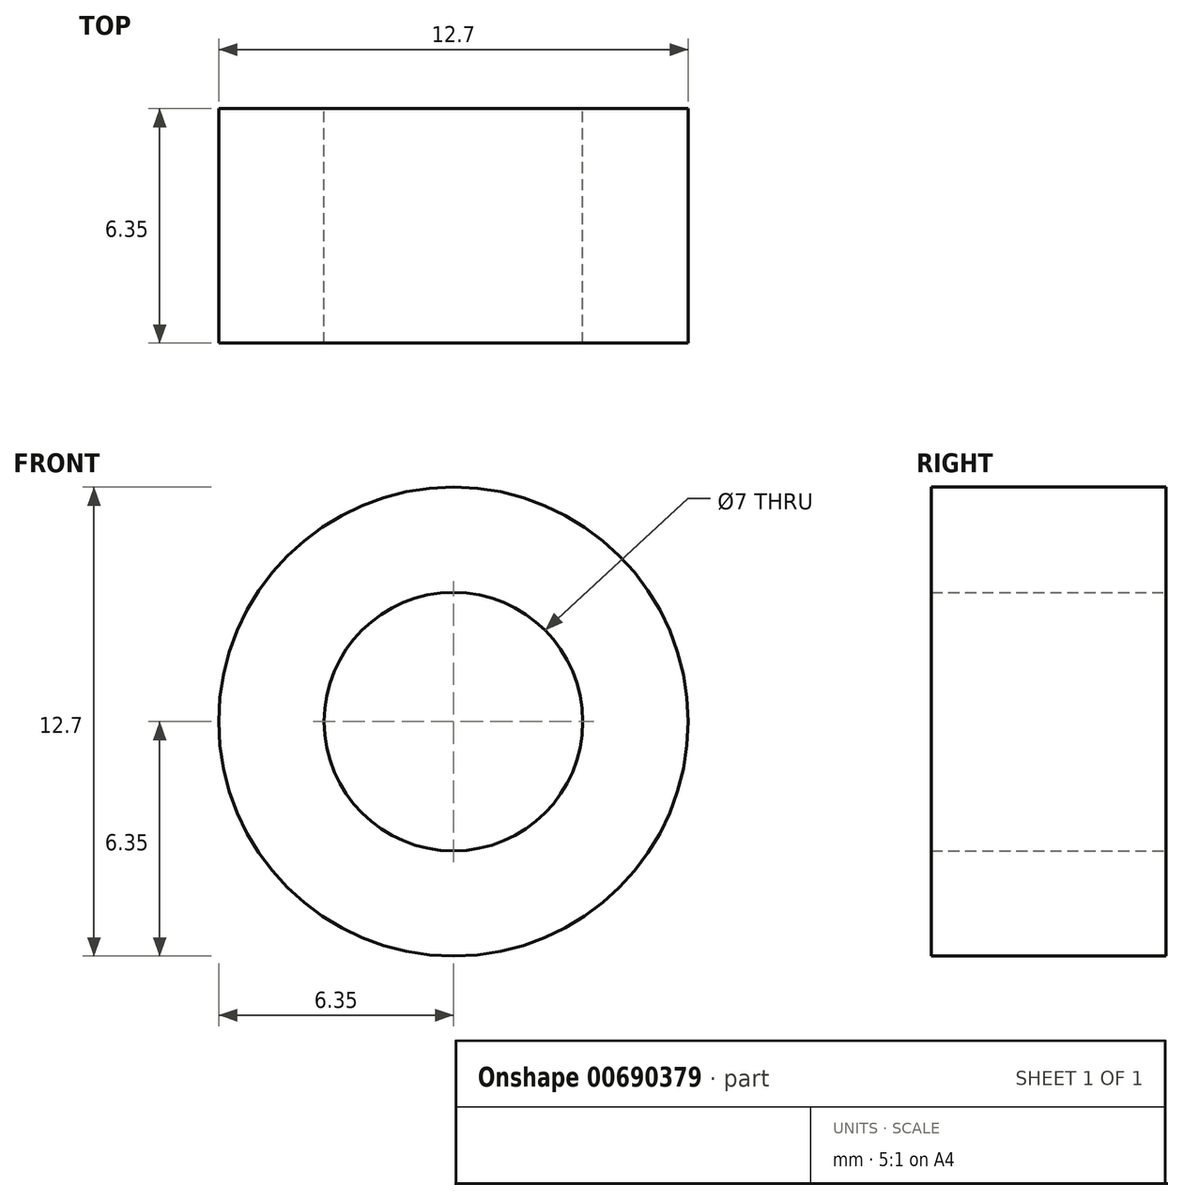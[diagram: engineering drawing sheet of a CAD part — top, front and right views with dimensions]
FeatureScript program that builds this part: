
annotation { "Feature Type Name" : "Feature", "Feature Type Description" : "" }
export const myFeature = defineFeature(function(context is Context, id is Id, definition is map)
    precondition{}
    {
        {
            var Q0;
            Q0=qCreatedBy(makeId("Front.planeOp"),FACE);
            var sketch = newSketch(context, id + "F0", { "sketchPlane" : qUnion([Q0])});
            skCircle(sketch, "E0", {"center": v(0, 0) * mm, "radius": 6.35 * mm});
            skCircle(sketch, "E1", {"center": v(0, 0) * mm, "radius": 3.5 * mm});
            skSolve(sketch);
        }
        {
            var Q0;
            Q0 = qSketchRegion(id + "F0", true);
            extrude(context, id + "F1", {"entities" : qUnion([Q0]), "depth" : 6.35 * mm, "offsetDistance" : 25.4 * mm});
        }
    });
